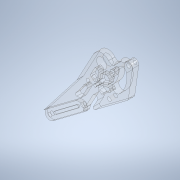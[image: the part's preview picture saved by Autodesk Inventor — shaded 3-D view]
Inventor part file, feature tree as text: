
AUTODESK INVENTOR PART (.ipt)
format: ipt  version: 2020.2 (Build 242310000, 310)  size: 979,456 bytes
history: native  units: mm
features: sketch x21, extrude x18, projected_geometry x13, other x6, hole x2, fillet x2
ambient origin geometry x8: Origin, YZ Plane, XZ Plane, XY Plane, X Axis, Y Axis, Z Axis, Center Point
bodies: Body1 (feature_tree)
feature tree (62):
  other  "ソリッド1"
  sketch  "スケッチ1"
  sketch  "スケッチ2"
  extrude  "押し出し1"  Depth=5.0mm TaperAngle=0.0deg
  hole  "穴1"  [1 undecoded]
  fillet  "フィレット1"  Radius=4.0mm
  extrude  "押し出し2"  Depth=5.0mm TaperAngle=0.0deg
  extrude  "押し出し3"  Depth=10.0mm TaperAngle=0.0deg
  extrude  "押し出し4"  Depth=1.0mm TaperAngle=0.0deg
  extrude  "押し出し5"  Depth=4.014257mm
  sketch  "スケッチ7"
  extrude  "押し出し6"  Depth=7.971681mm
  extrude  "押し出し7"  Depth=3.98584mm
  extrude  "押し出し8"  Depth=2.0mm TaperAngle=0.0deg
  sketch  "スケッチ9"
  extrude  "押し出し9"  Depth=4.0mm TaperAngle=0.0deg
  hole  "穴2"  [1 undecoded]
  sketch  "スケッチ10"
  extrude  "押し出し10"  Depth=6.5mm
  sketch  "スケッチ12"
  extrude  "押し出し11"  Depth=10.0mm TaperAngle=0.0deg
  extrude  "押し出し12"  Depth=7.0mm
  sketch  "スケッチ13"
  sketch  "スケッチ14"
  sketch  "スケッチ15"
  fillet  "フィレット2"  Radius=6.0mm
  sketch  "スケッチ16"
  sketch  "スケッチ17"
  extrude  "押し出し16"  Depth=5.0mm TaperAngle=0.0deg
  extrude  "押し出し17"  Depth=6.0mm TaperAngle=0.0deg
  sketch  "スケッチ20"
  extrude  "押し出し18"  Depth=2.0mm TaperAngle=0.0deg
  extrude  "押し出し19"  Depth=8.0mm
  extrude  "押し出し20"  Depth=8.0mm
  extrude  "押し出し21"  Depth=2.994121mm
  sketch  "スケッチ3"
  projected_geometry  "投影ループ1"
  sketch  "スケッチ4"
  projected_geometry  "投影ループ2"
  sketch  "スケッチ5"
  projected_geometry  "投影ループ3"
  sketch  "スケッチ6"
  projected_geometry  "投影ループ4"
  projected_geometry  "投影ループ5"
  sketch  "スケッチ8"
  projected_geometry  "投影ループ6"
  sketch  "スケッチ11"
  projected_geometry  "投影ループ7"
  projected_geometry  "投影ループ8"
  projected_geometry  "投影ループ9"
  projected_geometry  "投影ループ10"
  projected_geometry  "投影ループ11"
  sketch  "スケッチ18"
  projected_geometry  "投影ループ12"
  sketch  "スケッチ19"
  projected_geometry  "投影ループ13"
  sketch  "スケッチ21"
  other  "断面エッジを投影1"
  other  "断面エッジを投影2"
  other  "断面エッジを投影3"
  other  "断面エッジを投影4"
  other  "断面エッジを投影5"
note: 2 required parameter values undecoded (feature->parameter linkage not recoverable at this tier; creation-order binding heuristic only, values carry confidence <= 0.55)
